# Revit family: Dunbar 255 ETL
name_source: partatom
category: Lighting Fixtures
revit_build: Autodesk Revit 2018 (Build: 20170223_1515(x64)
units: mm (PartAtom-declared; Revit-internal decimal feet)

## family parameters
Always vertical = Yes
Cut with Voids When Loaded = No
Host = Wall
Light Source = Yes
OmniClass Number = 23.80.70.00
OmniClass Title = Lighting
Part Type = Normal
Room Calculation Point = No
Round Connector Dimension = Use Diameter
Shared = No

## types (4) — shared parameters
ADA compliant = NO
Color Filter = 16777215
Dimmable = No
Dimming Lamp Color Temperature Shift = <None>
Driver Included = Yes
Driver Required = No
Emit from Line Length = 610 mm
Lamp = LED
Length of Cable Supplied = 150mm
Light Source Fixed = Yes
Main Material = Metal - Aluminium
Manufacturer = Astro Lighting Ltd
Photometric Web File = GNC-21603 Dunbar 255 [ETL] Texture Black - 8083 inc sphere.ies
Tilt Angle = 90.00°
URL = www.astrolighting.com

## per-type parameters (varying)
| type | Efficacy (lm/w) | Electrical Class | Location rating | Main Finish | Power (Watts) | Product Code | Product Location | Product Name | Product SKU |
| ETL |  | 0 | DAMP |  |  | 1234 | Bathroom |  | 1234001 |
| Dunbar 255 White | 33 | 1 | WET | Textured White | 7.6 | 7991 | Outdoor | Dunbar 255 Textured White | 1298009 |
| Dunbar 255 Black | 33 | 1 | WET | Textured Black | 7.6 | 7989 | Outdoor | Dunbar 255 Textured Black | 1298007 |
| Dunbar 255 Grey | 33 | 1 | WET | Textured Grey | 7.6 | 8208 | Outdoor | Dunbar 255 Textured Grey | 1298023 |

## geometry (parser evidence)
native form markers: Sweep x3
no freeform markers — native parametric forms only
